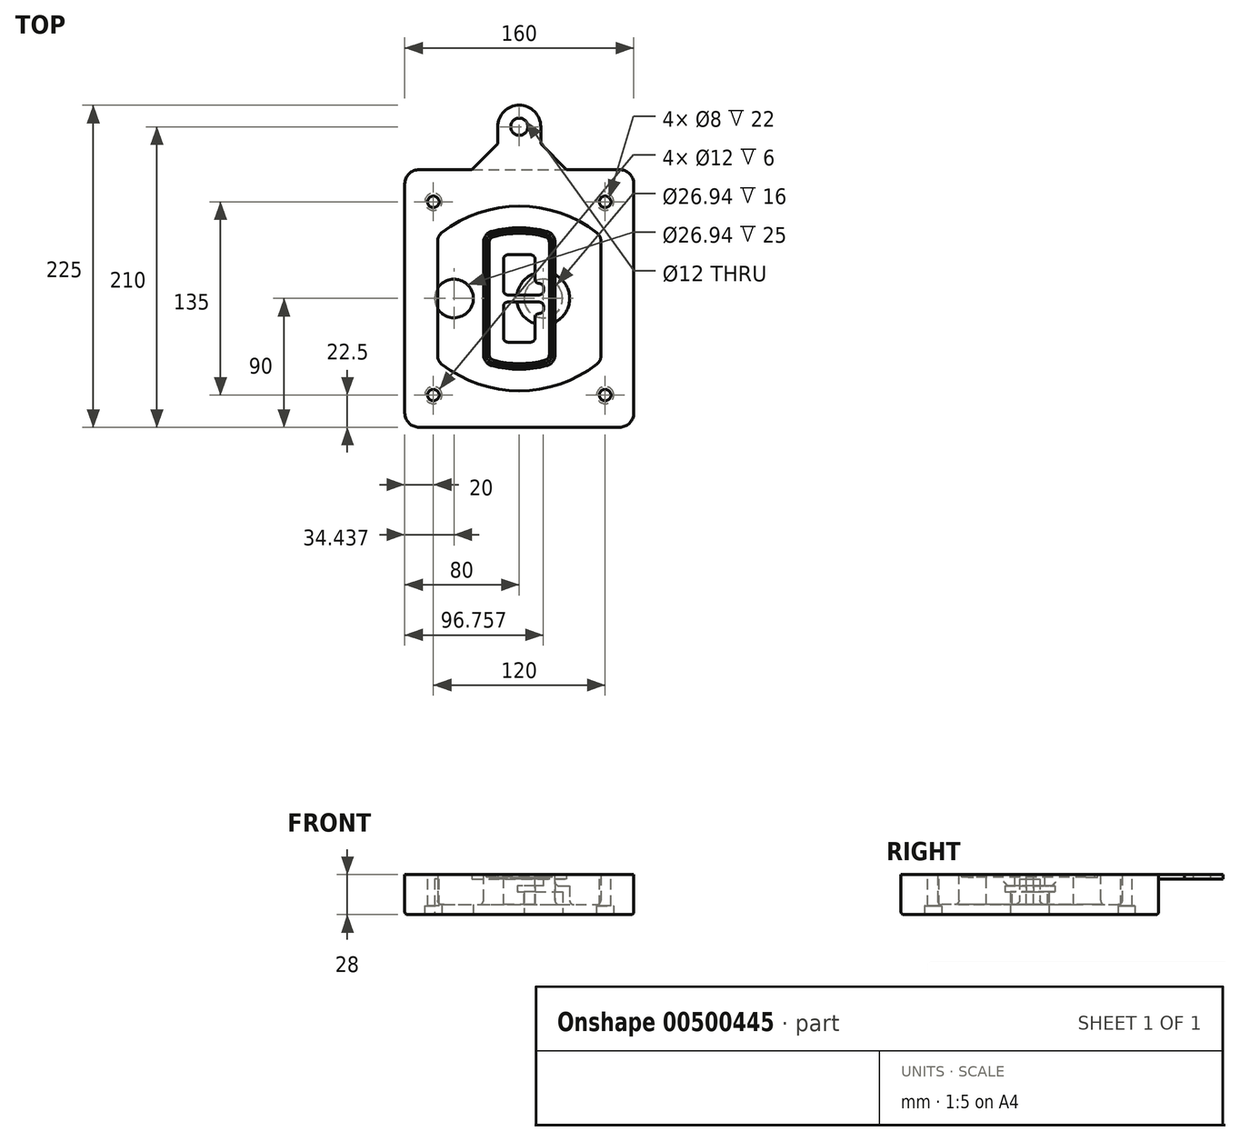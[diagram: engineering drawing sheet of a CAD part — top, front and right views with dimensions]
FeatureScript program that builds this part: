
annotation { "Feature Type Name" : "Feature", "Feature Type Description" : "" }
export const myFeature = defineFeature(function(context is Context, id is Id, definition is map)
    precondition{}
    {
        {
            var Q0;
            Q0=qCreatedBy(makeId("Top.planeOp"),FACE);
            var sketch = newSketch(context, id + "F0", { "sketchPlane" : qUnion([Q0])});
            skPoint(sketch, "E0.rect.middle", {"position": v(0, 0) * mm});
            skLineSegment(sketch, "E1.bottom", {"start": v(-70, -90) * mm, "end": v(70, -90) * mm});
            skLineSegment(sketch, "E1.top", {"start": v(-70, 90) * mm, "end": v(70, 90) * mm});
            skLineSegment(sketch, "E1.left", {"start": v(-80, -80) * mm, "end": v(-80, 80) * mm});
            skLineSegment(sketch, "E1.right", {"start": v(80, -80) * mm, "end": v(80, 80) * mm});
            skLineSegment(sketch, "E2", {"start": v(-80, 90) * mm, "end": v(80, -90) * mm, "construction": true});
            skLineSegment(sketch, "E3", {"start": v(80, 90) * mm, "end": v(-80, -90) * mm, "construction": true});
            skCircle(sketch, "E4", {"center": v(-60, 67.5) * mm, "radius": 4 * mm});
            skCircle(sketch, "E5", {"center": v(60, 67.5) * mm, "radius": 4 * mm});
            skCircle(sketch, "E6", {"center": v(60, -67.5) * mm, "radius": 4 * mm});
            skCircle(sketch, "E7", {"center": v(-60, -67.5) * mm, "radius": 4 * mm});
            skLineSegment(sketch, "E8", {"start": v(-60, 67.5) * mm, "end": v(60, 67.5) * mm, "construction": true});
            skLineSegment(sketch, "E9", {"start": v(60, 67.5) * mm, "end": v(60, -67.5) * mm, "construction": true});
            skLineSegment(sketch, "E10", {"start": v(60, -67.5) * mm, "end": v(-60, -67.5) * mm, "construction": true});
            skLineSegment(sketch, "E11", {"start": v(-60, -67.5) * mm, "end": v(-60, 67.5) * mm, "construction": true});
            skLineSegment(sketch, "E12", {"start": v(-60, 40.3) * mm, "end": v(-60, -40.3) * mm});
            skLineSegment(sketch, "E13", {"start": v(60, 40.3) * mm, "end": v(60, -40.3) * mm});
            skArc(sketch, "E14", {"start": v(56.15, 48.18) * mm, "mid": v(0, 67.5) * mm, "end": v(-56.15, 48.18) * mm});
            skArc(sketch, "E15", {"start": v(-56.15, -48.18) * mm, "mid": v(0, -67.5) * mm, "end": v(56.15, -48.18) * mm});
            skLineSegment(sketch, "E16", {"start": v(-60, 0) * mm, "end": v(60, 0) * mm, "construction": true});
            skPoint(sketch, "E17.visualSharp", {"position": v(-60, -45) * mm});
            skArc(sketch, "E17.filletArc", {"start": v(-60, -40.3) * mm, "mid": v(-58.99, -44.68) * mm, "end": v(-56.15, -48.18) * mm});
            skPoint(sketch, "E18.visualSharp", {"position": v(-60, 45) * mm});
            skArc(sketch, "E18.filletArc", {"start": v(-56.15, 48.18) * mm, "mid": v(-58.99, 44.68) * mm, "end": v(-60, 40.3) * mm});
            skPoint(sketch, "E19.visualSharp", {"position": v(60, 45) * mm});
            skArc(sketch, "E19.filletArc", {"start": v(60, 40.3) * mm, "mid": v(58.99, 44.68) * mm, "end": v(56.15, 48.18) * mm});
            skPoint(sketch, "E20.visualSharp", {"position": v(60, -45) * mm});
            skArc(sketch, "E20.filletArc", {"start": v(56.15, -48.18) * mm, "mid": v(58.99, -44.68) * mm, "end": v(60, -40.3) * mm});
            skPoint(sketch, "E21.visualSharp", {"position": v(-80, 90) * mm});
            skArc(sketch, "E21.filletArc", {"start": v(-70, 90) * mm, "mid": v(-77.07, 87.07) * mm, "end": v(-80, 80) * mm});
            skPoint(sketch, "E22.visualSharp", {"position": v(80, 90) * mm});
            skArc(sketch, "E22.filletArc", {"start": v(80, 80) * mm, "mid": v(77.07, 87.07) * mm, "end": v(70, 90) * mm});
            skPoint(sketch, "E23.visualSharp", {"position": v(80, -90) * mm});
            skArc(sketch, "E23.filletArc", {"start": v(70, -90) * mm, "mid": v(77.07, -87.07) * mm, "end": v(80, -80) * mm});
            skPoint(sketch, "E24.visualSharp", {"position": v(-80, -90) * mm});
            skArc(sketch, "E24.filletArc", {"start": v(-80, -80) * mm, "mid": v(-77.07, -87.07) * mm, "end": v(-70, -90) * mm});
            skArc(sketch, "E25.0", {"start": v(57, 40.3) * mm, "mid": v(56.3, 43.36) * mm, "end": v(54.3, 45.81) * mm});
            skLineSegment(sketch, "E25.1", {"start": v(57, 40.3) * mm, "end": v(57, -40.3) * mm});
            skArc(sketch, "E25.2", {"start": v(54.3, -45.81) * mm, "mid": v(56.3, -43.36) * mm, "end": v(57, -40.3) * mm});
            skArc(sketch, "E25.3", {"start": v(-54.3, -45.81) * mm, "mid": v(0, -64.5) * mm, "end": v(54.3, -45.81) * mm});
            skArc(sketch, "E25.4", {"start": v(-57, -40.3) * mm, "mid": v(-56.3, -43.36) * mm, "end": v(-54.3, -45.81) * mm});
            skArc(sketch, "E25.5", {"start": v(54.3, 45.81) * mm, "mid": v(0, 64.5) * mm, "end": v(-54.3, 45.81) * mm});
            skLineSegment(sketch, "E25.6", {"start": v(-57, 40.3) * mm, "end": v(-57, -40.3) * mm});
            skArc(sketch, "E25.7", {"start": v(-54.3, 45.81) * mm, "mid": v(-56.3, 43.36) * mm, "end": v(-57, 40.3) * mm});
            skArc(sketch, "E26.0", {"start": v(-58.62, 51.33) * mm, "mid": v(-62.58, 46.43) * mm, "end": v(-64, 40.3) * mm});
            skArc(sketch, "E26.1", {"start": v(58.62, 51.33) * mm, "mid": v(0, 71.5) * mm, "end": v(-58.62, 51.33) * mm});
            skArc(sketch, "E26.2", {"start": v(64, 40.3) * mm, "mid": v(62.58, 46.43) * mm, "end": v(58.62, 51.33) * mm});
            skLineSegment(sketch, "E26.3", {"start": v(64, 40.3) * mm, "end": v(64, -40.3) * mm});
            skArc(sketch, "E26.4", {"start": v(58.62, -51.33) * mm, "mid": v(62.58, -46.43) * mm, "end": v(64, -40.3) * mm});
            skLineSegment(sketch, "E26.5", {"start": v(-64, 40.3) * mm, "end": v(-64, -40.3) * mm});
            skArc(sketch, "E26.6", {"start": v(-58.62, -51.33) * mm, "mid": v(0, -71.5) * mm, "end": v(58.62, -51.33) * mm});
            skArc(sketch, "E26.7", {"start": v(-64, -40.3) * mm, "mid": v(-62.58, -46.43) * mm, "end": v(-58.62, -51.33) * mm});
            skSolve(sketch);
        }
        {
            var Q0;
            Q0=makeQuery(id+"F0.imprint","IMPRINT",FACE,{"disambiguationData":[TD([[makeQuery(id+"F0.imprint","IMPRINT",EDGE,{"derivedFrom":sQuery(id+"F0.wireOp",EDGE,"E1.bottom")}),1.0]])]});
            var Q1;
            Q1=makeQuery(id+"F0.imprint","IMPRINT",FACE,{"disambiguationData":[TD([[makeQuery(id+"F0.imprint","IMPRINT",EDGE,{"derivedFrom":sQuery(id+"F0.wireOp",EDGE,"E12")}),1.0]])]});
            var Q2;
            Q2=makeQuery(id+"F0.imprint","IMPRINT",FACE,{"disambiguationData":[TD([[makeQuery(id+"F0.imprint","IMPRINT",EDGE,{"derivedFrom":sQuery(id+"F0.wireOp",EDGE,"E25.0")}),1.0]])]});
            var Q3;
            Q3=makeQuery(id+"F0.imprint","IMPRINT",FACE,{"disambiguationData":[TD([[makeQuery(id+"F0.imprint","IMPRINT",EDGE,{"derivedFrom":sQuery(id+"F0.wireOp",EDGE,"E12")}),-1.0]])]});
            extrude(context, id + "F1", {"entities" : qUnion([Q0, Q1, Q2, Q3]), "oppositeDirection" : true, "depth" : 25 * mm});
        }
        {
            var Q0;
            Q0=makeQuery(id+"F0.imprint","IMPRINT",FACE,{"disambiguationData":[TD([[makeQuery(id+"F0.imprint","IMPRINT",EDGE,{"derivedFrom":sQuery(id+"F0.wireOp",EDGE,"E12")}),1.0]])]});
            extrude(context, id + "F2", {"entities" : qUnion([Q0]), "operationType" : NewBodyOperationType.ADD, "depth" : 3 * mm});
        }
        {
            var Q0;
            Q0=makeQuery(id+"F0.imprint","IMPRINT",FACE,{"disambiguationData":[TD([[makeQuery(id+"F0.imprint","IMPRINT",EDGE,{"derivedFrom":sQuery(id+"F0.wireOp",EDGE,"E25.0")}),1.0]])]});
            extrude(context, id + "F3", {"entities" : qUnion([Q0]), "operationType" : NewBodyOperationType.REMOVE, "oppositeDirection" : true, "depth" : 18 * mm});
        }
        {
            var Q0;
            Q0=makeQuery(id+"F2.opExtrude","CAP_FACE",FACE,{"disambiguationData":[OSD([sQuery(id+"F0.wireOp",EDGE,"E12"),sQuery(id+"F0.wireOp",EDGE,"E13"),sQuery(id+"F0.wireOp",EDGE,"E14"),sQuery(id+"F0.wireOp",EDGE,"E15"),sQuery(id+"F0.wireOp",EDGE,"E17.filletArc"),sQuery(id+"F0.wireOp",EDGE,"E18.filletArc"),sQuery(id+"F0.wireOp",EDGE,"E19.filletArc"),sQuery(id+"F0.wireOp",EDGE,"E20.filletArc"),sQuery(id+"F0.wireOp",EDGE,"E25.0"),sQuery(id+"F0.wireOp",EDGE,"E25.1"),sQuery(id+"F0.wireOp",EDGE,"E25.2"),sQuery(id+"F0.wireOp",EDGE,"E25.3"),sQuery(id+"F0.wireOp",EDGE,"E25.4"),sQuery(id+"F0.wireOp",EDGE,"E25.5"),sQuery(id+"F0.wireOp",EDGE,"E25.6"),sQuery(id+"F0.wireOp",EDGE,"E25.7")])],"isStart":false});
            var sketch = newSketch(context, id + "F4", { "sketchPlane" : qUnion([Q0])});
            skArc(sketch, "E27.0", {"start": v(-19.08, -46.97) * mm, "mid": v(0, -49.5) * mm, "end": v(19.08, -46.97) * mm});
            skArc(sketch, "E28.0", {"start": v(19.08, 46.97) * mm, "mid": v(0, 49.5) * mm, "end": v(-19.08, 46.97) * mm});
            skLineSegment(sketch, "E29", {"start": v(-25, 39.25) * mm, "end": v(-25, -39.25) * mm});
            skLineSegment(sketch, "E30", {"start": v(25, 39.25) * mm, "end": v(25, -39.25) * mm});
            skLineSegment(sketch, "E31", {"start": v(-25, 45.1) * mm, "end": v(25, 45.1) * mm, "construction": true});
            skLineSegment(sketch, "E32", {"start": v(-25, -45.1) * mm, "end": v(25, -45.1) * mm, "construction": true});
            skPoint(sketch, "E33.visualSharp", {"position": v(-25, 45.1) * mm});
            skArc(sketch, "E33.filletArc", {"start": v(-19.08, 46.97) * mm, "mid": v(-23.35, 44.11) * mm, "end": v(-25, 39.25) * mm});
            skPoint(sketch, "E34.visualSharp", {"position": v(25, 45.1) * mm});
            skArc(sketch, "E34.filletArc", {"start": v(25, 39.25) * mm, "mid": v(23.35, 44.11) * mm, "end": v(19.08, 46.97) * mm});
            skPoint(sketch, "E35.visualSharp", {"position": v(25, -45.1) * mm});
            skArc(sketch, "E35.filletArc", {"start": v(19.08, -46.97) * mm, "mid": v(23.35, -44.11) * mm, "end": v(25, -39.25) * mm});
            skPoint(sketch, "E36.visualSharp", {"position": v(-25, -45.1) * mm});
            skArc(sketch, "E36.filletArc", {"start": v(-25, -39.25) * mm, "mid": v(-23.35, -44.11) * mm, "end": v(-19.08, -46.97) * mm});
            skArc(sketch, "E37.0", {"start": v(54.3, 45.81) * mm, "mid": v(0, 64.5) * mm, "end": v(-54.3, 45.81) * mm});
            skArc(sketch, "E37.1", {"start": v(-54.3, 45.81) * mm, "mid": v(-56.3, 43.36) * mm, "end": v(-57, 40.3) * mm});
            skLineSegment(sketch, "E37.2", {"start": v(-57, 40.3) * mm, "end": v(-57, -40.3) * mm});
            skArc(sketch, "E37.3", {"start": v(-57, -40.3) * mm, "mid": v(-56.3, -43.36) * mm, "end": v(-54.3, -45.81) * mm});
            skArc(sketch, "E37.4", {"start": v(-54.3, -45.81) * mm, "mid": v(0, -64.5) * mm, "end": v(54.3, -45.81) * mm});
            skArc(sketch, "E37.5", {"start": v(54.3, -45.81) * mm, "mid": v(56.3, -43.36) * mm, "end": v(57, -40.3) * mm});
            skLineSegment(sketch, "E37.6", {"start": v(57, 40.3) * mm, "end": v(57, -40.3) * mm});
            skArc(sketch, "E37.7", {"start": v(57, 40.3) * mm, "mid": v(56.3, 43.36) * mm, "end": v(54.3, 45.81) * mm});
            skLineSegment(sketch, "E38.0", {"start": v(23, 39.25) * mm, "end": v(23, -39.25) * mm});
            skArc(sketch, "E38.1", {"start": v(18.56, -45.04) * mm, "mid": v(21.76, -42.9) * mm, "end": v(23, -39.25) * mm});
            skArc(sketch, "E38.2", {"start": v(-18.56, -45.04) * mm, "mid": v(0, -47.5) * mm, "end": v(18.56, -45.04) * mm});
            skArc(sketch, "E38.3", {"start": v(-23, -39.25) * mm, "mid": v(-21.76, -42.9) * mm, "end": v(-18.56, -45.04) * mm});
            skLineSegment(sketch, "E38.4", {"start": v(-23, 39.25) * mm, "end": v(-23, -39.25) * mm});
            skArc(sketch, "E38.5", {"start": v(23, 39.25) * mm, "mid": v(21.76, 42.9) * mm, "end": v(18.56, 45.04) * mm});
            skArc(sketch, "E38.6", {"start": v(-18.56, 45.04) * mm, "mid": v(-21.76, 42.9) * mm, "end": v(-23, 39.25) * mm});
            skArc(sketch, "E38.7", {"start": v(18.56, 45.04) * mm, "mid": v(0, 47.5) * mm, "end": v(-18.56, 45.04) * mm});
            skArc(sketch, "E39.0", {"start": v(21, 39.25) * mm, "mid": v(20.18, 41.68) * mm, "end": v(18.04, 43.1) * mm});
            skLineSegment(sketch, "E39.1", {"start": v(21, 39.25) * mm, "end": v(21, -39.25) * mm});
            skArc(sketch, "E39.2", {"start": v(18.04, -43.1) * mm, "mid": v(20.18, -41.68) * mm, "end": v(21, -39.25) * mm});
            skArc(sketch, "E39.3", {"start": v(-18.04, -43.1) * mm, "mid": v(0, -45.5) * mm, "end": v(18.04, -43.1) * mm});
            skArc(sketch, "E39.4", {"start": v(-21, -39.25) * mm, "mid": v(-20.18, -41.68) * mm, "end": v(-18.04, -43.1) * mm});
            skArc(sketch, "E39.5", {"start": v(18.04, 43.1) * mm, "mid": v(0, 45.5) * mm, "end": v(-18.04, 43.1) * mm});
            skLineSegment(sketch, "E39.6", {"start": v(-21, 39.25) * mm, "end": v(-21, -39.25) * mm});
            skArc(sketch, "E39.7", {"start": v(-18.04, 43.1) * mm, "mid": v(-20.18, 41.68) * mm, "end": v(-21, 39.25) * mm});
            skLineSegment(sketch, "E40", {"start": v(-25, 0) * mm, "end": v(25, 0) * mm, "construction": true});
            skLineSegment(sketch, "E41", {"start": v(-11, 5.5) * mm, "end": v(-11, 27.5) * mm});
            skLineSegment(sketch, "E42", {"start": v(-8, 30.5) * mm, "end": v(8, 30.5) * mm});
            skLineSegment(sketch, "E43", {"start": v(11, 27.5) * mm, "end": v(11, 13.5) * mm});
            skLineSegment(sketch, "E44", {"start": v(14, 10.5) * mm, "end": v(14, 10.5) * mm});
            skLineSegment(sketch, "E45", {"start": v(17, 7.5) * mm, "end": v(17, 5.5) * mm});
            skLineSegment(sketch, "E46", {"start": v(14, 2.5) * mm, "end": v(-8, 2.5) * mm});
            skPoint(sketch, "E47.visualSharp", {"position": v(-11, 30.5) * mm});
            skArc(sketch, "E47.filletArc", {"start": v(-8, 30.5) * mm, "mid": v(-10.12, 29.62) * mm, "end": v(-11, 27.5) * mm});
            skPoint(sketch, "E48.visualSharp", {"position": v(11, 30.5) * mm});
            skArc(sketch, "E48.filletArc", {"start": v(11, 27.5) * mm, "mid": v(10.12, 29.62) * mm, "end": v(8, 30.5) * mm});
            skPoint(sketch, "E49.visualSharp", {"position": v(11, 10.5) * mm});
            skArc(sketch, "E49.filletArc", {"start": v(11, 13.5) * mm, "mid": v(11.88, 11.38) * mm, "end": v(14, 10.5) * mm});
            skPoint(sketch, "E50.visualSharp", {"position": v(17, 10.5) * mm});
            skArc(sketch, "E50.filletArc", {"start": v(17, 7.5) * mm, "mid": v(16.12, 9.62) * mm, "end": v(14, 10.5) * mm});
            skPoint(sketch, "E51.visualSharp", {"position": v(17, 2.5) * mm});
            skArc(sketch, "E51.filletArc", {"start": v(14, 2.5) * mm, "mid": v(16.12, 3.38) * mm, "end": v(17, 5.5) * mm});
            skPoint(sketch, "E52.visualSharp", {"position": v(-11, 2.5) * mm});
            skArc(sketch, "E52.filletArc", {"start": v(-11, 5.5) * mm, "mid": v(-10.12, 3.38) * mm, "end": v(-8, 2.5) * mm});
            skLineSegment(sketch, "E53.0.MirrorCS", {"start": v(14, -2.5) * mm, "end": v(-8, -2.5) * mm});
            skArc(sketch, "E54.0.MirrorCS", {"start": v(-11, -5.5) * mm, "mid": v(-10.12, -3.38) * mm, "end": v(-8, -2.5) * mm});
            skLineSegment(sketch, "E55.0.MirrorCS", {"start": v(-11, -5.5) * mm, "end": v(-11, -27.5) * mm});
            skArc(sketch, "E56.0.MirrorCS", {"start": v(-8, -30.5) * mm, "mid": v(-10.12, -29.62) * mm, "end": v(-11, -27.5) * mm});
            skLineSegment(sketch, "E57.0.MirrorCS", {"start": v(-8, -30.5) * mm, "end": v(8, -30.5) * mm});
            skArc(sketch, "E58.0.MirrorCS", {"start": v(11, -27.5) * mm, "mid": v(10.12, -29.62) * mm, "end": v(8, -30.5) * mm});
            skLineSegment(sketch, "E59.0.MirrorCS", {"start": v(11, -27.5) * mm, "end": v(11, -13.5) * mm});
            skArc(sketch, "E60.0.MirrorCS", {"start": v(11, -13.5) * mm, "mid": v(11.88, -11.38) * mm, "end": v(14, -10.5) * mm});
            skArc(sketch, "E61.0.MirrorCS", {"start": v(17, -7.5) * mm, "mid": v(16.12, -9.62) * mm, "end": v(14, -10.5) * mm});
            skLineSegment(sketch, "E62.0.MirrorCS", {"start": v(17, -7.5) * mm, "end": v(17, -5.5) * mm});
            skArc(sketch, "E63.0.MirrorCS", {"start": v(14, -2.5) * mm, "mid": v(16.12, -3.38) * mm, "end": v(17, -5.5) * mm});
            skSolve(sketch);
        }
        {
            var Q0;
            Q0=makeQuery(id+"F4.imprint","IMPRINT",FACE,{"disambiguationData":[TD([[makeQuery(id+"F4.imprint","IMPRINT",EDGE,{"derivedFrom":sQuery(id+"F4.wireOp",EDGE,"E27.0")}),1.0]])]});
            var Q1;
            Q1=makeQuery(id+"F4.imprint","IMPRINT",FACE,{"disambiguationData":[TD([[makeQuery(id+"F4.imprint","IMPRINT",EDGE,{"derivedFrom":sQuery(id+"F4.wireOp",EDGE,"E38.0")}),-1.0]])]});
            var Q2;
            Q2=makeQuery(id+"F4.imprint","IMPRINT",FACE,{"disambiguationData":[TD([[makeQuery(id+"F4.imprint","IMPRINT",EDGE,{"derivedFrom":sQuery(id+"F4.wireOp",EDGE,"E39.0")}),1.0]])]});
            extrude(context, id + "F5", {"entities" : qUnion([Q0, Q1, Q2]), "operationType" : NewBodyOperationType.ADD, "endBound" : BoundingType.UP_TO_NEXT, "oppositeDirection" : true, "depth" : 25 * mm});
        }
        {
            var Q0;
            Q0=makeQuery(id+"F4.imprint","IMPRINT",FACE,{"disambiguationData":[TD([[makeQuery(id+"F4.imprint","IMPRINT",EDGE,{"derivedFrom":sQuery(id+"F4.wireOp",EDGE,"E38.0")}),-1.0]])]});
            extrude(context, id + "F6", {"entities" : qUnion([Q0]), "operationType" : NewBodyOperationType.REMOVE, "oppositeDirection" : true, "depth" : 2 * mm});
        }
        {
            var Q0;
            Q0=makeQuery(id+"F1.opExtrude","CAP_FACE",FACE,{"disambiguationData":[OSD([sQuery(id+"F0.wireOp",EDGE,"E1.bottom"),sQuery(id+"F0.wireOp",EDGE,"E1.top"),sQuery(id+"F0.wireOp",EDGE,"E1.left"),sQuery(id+"F0.wireOp",EDGE,"E1.right"),sQuery(id+"F0.wireOp",EDGE,"E4"),sQuery(id+"F0.wireOp",EDGE,"E5"),sQuery(id+"F0.wireOp",EDGE,"E6"),sQuery(id+"F0.wireOp",EDGE,"E7"),sQuery(id+"F0.wireOp",EDGE,"E21.filletArc"),sQuery(id+"F0.wireOp",EDGE,"E22.filletArc"),sQuery(id+"F0.wireOp",EDGE,"E23.filletArc"),sQuery(id+"F0.wireOp",EDGE,"E24.filletArc")])],"isStart":false});
            var sketch = newSketch(context, id + "F7", { "sketchPlane" : qUnion([Q0])});
            skCircle(sketch, "E64", {"center": v(16.76, 0) * mm, "radius": 13.47 * mm});
            skCircle(sketch, "E65", {"center": v(-45.56, 0) * mm, "radius": 13.47 * mm});
            skLineSegment(sketch, "E66", {"start": v(80, 0) * mm, "end": v(-80, 0) * mm});
            skCircle(sketch, "E67", {"center": v(16.76, 0) * mm, "radius": 18.47 * mm});
            skCircle(sketch, "E68", {"center": v(60, -67.5) * mm, "radius": 6 * mm});
            skCircle(sketch, "E69", {"center": v(-60, -67.5) * mm, "radius": 6 * mm});
            skCircle(sketch, "E70", {"center": v(-60, 67.5) * mm, "radius": 6 * mm});
            skCircle(sketch, "E71", {"center": v(60, 67.5) * mm, "radius": 6 * mm});
            skSolve(sketch);
        }
        {
            var Q0;
            {var subQ1=sQuery(id+"F7.wireOp",EDGE,"E66");var subQ4=sQuery(id+"F7.wireOp",EDGE,"E64");var subQ6=makeQuery(id+"F7.imprint","INTERSECT",VERTEX,{"disambiguationData":[OD(0.0)],"derivedFrom":[subQ4,subQ1]});Q0=makeQuery(id+"F7.imprint","IMPRINT",FACE,{"disambiguationData":[TD([[makeQuery(id+"F7.imprint","IMPRINT",EDGE,{"disambiguationData":[TD([[subQ6,-1.0]])],"derivedFrom":subQ4}),-1.0]])]});}
            var Q1;
            {var subQ0=sQuery(id+"F7.wireOp",EDGE,"E66");var subQ1=sQuery(id+"F7.wireOp",EDGE,"E64");var subQ3=makeQuery(id+"F7.imprint","INTERSECT",VERTEX,{"disambiguationData":[OD(0.0)],"derivedFrom":[subQ1,subQ0]});Q1=makeQuery(id+"F7.imprint","IMPRINT",FACE,{"disambiguationData":[TD([[makeQuery(id+"F7.imprint","IMPRINT",EDGE,{"disambiguationData":[TD([[subQ3,-1.0]])],"derivedFrom":subQ1}),1.0]])]});}
            var Q2;
            {var subQ0=sQuery(id+"F7.wireOp",EDGE,"E66");var subQ1=sQuery(id+"F7.wireOp",EDGE,"E64");var subQ3=makeQuery(id+"F7.imprint","INTERSECT",VERTEX,{"disambiguationData":[OD(0.0)],"derivedFrom":[subQ1,subQ0]});Q2=makeQuery(id+"F7.imprint","IMPRINT",FACE,{"disambiguationData":[TD([[makeQuery(id+"F7.imprint","IMPRINT",EDGE,{"disambiguationData":[TD([[subQ3,1.0]])],"derivedFrom":subQ1}),1.0]])]});}
            var Q3;
            {var subQ1=sQuery(id+"F7.wireOp",EDGE,"E66");var subQ4=sQuery(id+"F7.wireOp",EDGE,"E64");var subQ6=makeQuery(id+"F7.imprint","INTERSECT",VERTEX,{"disambiguationData":[OD(0.0)],"derivedFrom":[subQ4,subQ1]});Q3=makeQuery(id+"F7.imprint","IMPRINT",FACE,{"disambiguationData":[TD([[makeQuery(id+"F7.imprint","IMPRINT",EDGE,{"disambiguationData":[TD([[subQ6,1.0]])],"derivedFrom":subQ4}),-1.0]])]});}
            extrude(context, id + "F8", {"entities" : qUnion([Q0, Q1, Q2, Q3]), "operationType" : NewBodyOperationType.ADD, "oppositeDirection" : true, "depth" : 20 * mm});
        }
        {
            var Q0;
            {var subQ0=sQuery(id+"F7.wireOp",EDGE,"E66");var subQ1=sQuery(id+"F7.wireOp",EDGE,"E64");var subQ3=makeQuery(id+"F7.imprint","INTERSECT",VERTEX,{"disambiguationData":[OD(0.0)],"derivedFrom":[subQ1,subQ0]});Q0=makeQuery(id+"F7.imprint","IMPRINT",FACE,{"disambiguationData":[TD([[makeQuery(id+"F7.imprint","IMPRINT",EDGE,{"disambiguationData":[TD([[subQ3,-1.0]])],"derivedFrom":subQ1}),1.0]])]});}
            var Q1;
            {var subQ0=sQuery(id+"F7.wireOp",EDGE,"E66");var subQ1=sQuery(id+"F7.wireOp",EDGE,"E64");var subQ3=makeQuery(id+"F7.imprint","INTERSECT",VERTEX,{"disambiguationData":[OD(0.0)],"derivedFrom":[subQ1,subQ0]});Q1=makeQuery(id+"F7.imprint","IMPRINT",FACE,{"disambiguationData":[TD([[makeQuery(id+"F7.imprint","IMPRINT",EDGE,{"disambiguationData":[TD([[subQ3,1.0]])],"derivedFrom":subQ1}),1.0]])]});}
            extrude(context, id + "F9", {"entities" : qUnion([Q0, Q1]), "operationType" : NewBodyOperationType.REMOVE, "oppositeDirection" : true, "depth" : 16 * mm});
        }
        {
            var Q0;
            {var subQ0=sQuery(id+"F7.wireOp",EDGE,"E66");var subQ1=sQuery(id+"F7.wireOp",EDGE,"E65");var subQ3=makeQuery(id+"F7.imprint","INTERSECT",VERTEX,{"disambiguationData":[OD(0.0)],"derivedFrom":[subQ1,subQ0]});Q0=makeQuery(id+"F7.imprint","IMPRINT",FACE,{"disambiguationData":[TD([[makeQuery(id+"F7.imprint","IMPRINT",EDGE,{"disambiguationData":[TD([[subQ3,-1.0]])],"derivedFrom":subQ1}),1.0]])]});}
            var Q1;
            {var subQ0=sQuery(id+"F7.wireOp",EDGE,"E66");var subQ1=sQuery(id+"F7.wireOp",EDGE,"E65");var subQ3=makeQuery(id+"F7.imprint","INTERSECT",VERTEX,{"disambiguationData":[OD(0.0)],"derivedFrom":[subQ1,subQ0]});Q1=makeQuery(id+"F7.imprint","IMPRINT",FACE,{"disambiguationData":[TD([[makeQuery(id+"F7.imprint","IMPRINT",EDGE,{"disambiguationData":[TD([[subQ3,1.0]])],"derivedFrom":subQ1}),1.0]])]});}
            extrude(context, id + "F10", {"entities" : qUnion([Q0, Q1]), "operationType" : NewBodyOperationType.REMOVE, "oppositeDirection" : true, "depth" : 25 * mm});
        }
        {
            var Q0;
            Q0=makeQuery(id+"F7.imprint","IMPRINT",FACE,{"disambiguationData":[TD([[makeQuery(id+"F7.imprint","IMPRINT",EDGE,{"derivedFrom":sQuery(id+"F7.wireOp",EDGE,"E68")}),1.0]])]});
            var Q1;
            Q1=makeQuery(id+"F7.imprint","IMPRINT",FACE,{"disambiguationData":[TD([[makeQuery(id+"F7.imprint","IMPRINT",EDGE,{"derivedFrom":makeQuery(id+"F1.opExtrude","CAP_EDGE",EDGE,{"disambiguationData":[OSD([sQuery(id+"F0.wireOp",EDGE,"E5")])],"isStart":false})}),-1.0]])]});
            var Q2;
            Q2=makeQuery(id+"F7.imprint","IMPRINT",FACE,{"disambiguationData":[TD([[makeQuery(id+"F7.imprint","IMPRINT",EDGE,{"derivedFrom":sQuery(id+"F7.wireOp",EDGE,"E69")}),1.0]])]});
            var Q3;
            Q3=makeQuery(id+"F7.imprint","IMPRINT",FACE,{"disambiguationData":[TD([[makeQuery(id+"F7.imprint","IMPRINT",EDGE,{"derivedFrom":makeQuery(id+"F1.opExtrude","CAP_EDGE",EDGE,{"disambiguationData":[OSD([sQuery(id+"F0.wireOp",EDGE,"E4")])],"isStart":false})}),-1.0]])]});
            var Q4;
            Q4=makeQuery(id+"F7.imprint","IMPRINT",FACE,{"disambiguationData":[TD([[makeQuery(id+"F7.imprint","IMPRINT",EDGE,{"derivedFrom":sQuery(id+"F7.wireOp",EDGE,"E70")}),1.0]])]});
            var Q5;
            Q5=makeQuery(id+"F7.imprint","IMPRINT",FACE,{"disambiguationData":[TD([[makeQuery(id+"F7.imprint","IMPRINT",EDGE,{"derivedFrom":makeQuery(id+"F1.opExtrude","CAP_EDGE",EDGE,{"disambiguationData":[OSD([sQuery(id+"F0.wireOp",EDGE,"E7")])],"isStart":false})}),-1.0]])]});
            var Q6;
            Q6=makeQuery(id+"F7.imprint","IMPRINT",FACE,{"disambiguationData":[TD([[makeQuery(id+"F7.imprint","IMPRINT",EDGE,{"derivedFrom":sQuery(id+"F7.wireOp",EDGE,"E71")}),1.0]])]});
            var Q7;
            Q7=makeQuery(id+"F7.imprint","IMPRINT",FACE,{"disambiguationData":[TD([[makeQuery(id+"F7.imprint","IMPRINT",EDGE,{"derivedFrom":makeQuery(id+"F1.opExtrude","CAP_EDGE",EDGE,{"disambiguationData":[OSD([sQuery(id+"F0.wireOp",EDGE,"E6")])],"isStart":false})}),-1.0]])]});
            extrude(context, id + "F11", {"entities" : qUnion([Q0, Q1, Q2, Q3, Q4, Q5, Q6, Q7]), "operationType" : NewBodyOperationType.REMOVE, "oppositeDirection" : true, "depth" : 6 * mm});
        }
        {
            var Q0;
            Q0=makeQuery(id+"F9.boolean.opBoolean","COPY",FACE,{"derivedFrom":makeQuery(id+"F9.opExtrude","CAP_FACE",FACE,{"disambiguationData":[OSD([sQuery(id+"F7.wireOp",EDGE,"E64")])],"isStart":false})});
            var sketch = newSketch(context, id + "F12", { "sketchPlane" : qUnion([Q0])});
            skArc(sketch, "E72.0", {"start": v(11, 17.55) * mm, "mid": v(2.57, 11.82) * mm, "end": v(-1.54, 2.5) * mm});
            skArc(sketch, "E72.1", {"start": v(-1.54, -2.5) * mm, "mid": v(2.57, -11.82) * mm, "end": v(11, -17.55) * mm});
            skLineSegment(sketch, "E73", {"start": v(-1.54, -2.5) * mm, "end": v(14, -2.5) * mm});
            skLineSegment(sketch, "E74.0", {"start": v(14, 2.5) * mm, "end": v(-1.54, 2.5) * mm});
            skArc(sketch, "E74.1", {"start": v(14, 2.5) * mm, "mid": v(16.12, 3.38) * mm, "end": v(17, 5.5) * mm});
            skLineSegment(sketch, "E74.2", {"start": v(17, 7.5) * mm, "end": v(17, 5.5) * mm});
            skArc(sketch, "E74.3", {"start": v(17, 7.5) * mm, "mid": v(16.12, 9.62) * mm, "end": v(14, 10.5) * mm});
            skArc(sketch, "E74.4", {"start": v(11, 13.5) * mm, "mid": v(11.88, 11.38) * mm, "end": v(14, 10.5) * mm});
            skLineSegment(sketch, "E74.5", {"start": v(11, 17.55) * mm, "end": v(11, 13.5) * mm});
            skLineSegment(sketch, "E74.7", {"start": v(14, -2.5) * mm, "end": v(-1.54, -2.5) * mm});
            skArc(sketch, "E74.8", {"start": v(14, -2.5) * mm, "mid": v(16.12, -3.38) * mm, "end": v(17, -5.5) * mm});
            skLineSegment(sketch, "E74.9", {"start": v(17, -7.5) * mm, "end": v(17, -5.5) * mm});
            skArc(sketch, "E74.10", {"start": v(17, -7.5) * mm, "mid": v(16.12, -9.62) * mm, "end": v(14, -10.5) * mm});
            skArc(sketch, "E74.11", {"start": v(11, -13.5) * mm, "mid": v(11.88, -11.38) * mm, "end": v(14, -10.5) * mm});
            skLineSegment(sketch, "E74.12", {"start": v(11, -17.55) * mm, "end": v(11, -13.5) * mm});
            skPoint(sketch, "E75.orphan", {"position": v(11, -27.5) * mm});
            skPoint(sketch, "E76.orphan", {"position": v(-8, -2.5) * mm});
            skPoint(sketch, "E77.orphan", {"position": v(-8, 2.5) * mm});
            skPoint(sketch, "E78.orphan", {"position": v(11, 27.5) * mm});
            skSolve(sketch);
        }
        {
            var Q0;
            {var subQ7=sQuery(id+"F12.wireOp",EDGE,"E72.0");var subQ14=sQuery(id+"F12.wireOp",EDGE,"E72.1");var subQ16=sQuery(id+"F12.wireOp",EDGE,"E74.1");var subQ18=sQuery(id+"F12.wireOp",EDGE,"E74.8");Q0=qUnion([makeQuery(id+"F12.imprint","IMPRINT",FACE,{"disambiguationData":[TD([[makeQuery(id+"F12.imprint","IMPRINT",EDGE,{"derivedFrom":subQ7}),1.0]])]}),makeQuery(id+"F12.imprint","IMPRINT",FACE,{"disambiguationData":[TD([[makeQuery(id+"F12.imprint","IMPRINT",EDGE,{"derivedFrom":subQ14}),1.0]])]}),makeQuery(id+"F12.imprint","IMPRINT",FACE,{"disambiguationData":[TD([[makeQuery(id+"F12.imprint","IMPRINT",EDGE,{"derivedFrom":subQ16}),1.0]])]}),makeQuery(id+"F12.imprint","IMPRINT",FACE,{"disambiguationData":[TD([[makeQuery(id+"F12.imprint","IMPRINT",EDGE,{"derivedFrom":subQ18}),-1.0]])]})]);}
            var Q1;
            Q1=makeQuery(id+"F5.boolean.opBoolean","SPLIT",FACE,{"disambiguationData":[TD([makeQuery(id+"F5.opExtrude","SWEPT_FACE",FACE,{"disambiguationData":[OSD([sQuery(id+"F4.wireOp",EDGE,"E41")])]})])],"derivedFrom":makeQuery(id+"F3.boolean.opBoolean","COPY",FACE,{"derivedFrom":makeQuery(id+"F3.opExtrude","CAP_FACE",FACE,{"disambiguationData":[OSD([sQuery(id+"F0.wireOp",EDGE,"E25.0"),sQuery(id+"F0.wireOp",EDGE,"E25.1"),sQuery(id+"F0.wireOp",EDGE,"E25.2"),sQuery(id+"F0.wireOp",EDGE,"E25.3"),sQuery(id+"F0.wireOp",EDGE,"E25.4"),sQuery(id+"F0.wireOp",EDGE,"E25.5"),sQuery(id+"F0.wireOp",EDGE,"E25.6"),sQuery(id+"F0.wireOp",EDGE,"E25.7")])],"isStart":false})})});
            extrude(context, id + "F13", {"entities" : qUnion([Q0]), "operationType" : NewBodyOperationType.REMOVE, "endBound" : BoundingType.UP_TO_SURFACE, "endBoundEntityFace" : qUnion([Q1]), "depth" : 25 * mm});
        }
        {
            var Q0;
            Q0=makeQuery(id+"F3.boolean.opBoolean","COPY",EDGE,{"derivedFrom":makeQuery(id+"F3.opExtrude","CAP_EDGE",EDGE,{"disambiguationData":[OSD([sQuery(id+"F0.wireOp",EDGE,"E25.6")])],"isStart":false})});
            var Q1;
            Q1=makeQuery(id+"F8.boolean.opBoolean","INTERSECT",EDGE,{"derivedFrom":[makeQuery(id+"F5.opExtrude","SWEPT_FACE",FACE,{"disambiguationData":[OSD([sQuery(id+"F4.wireOp",EDGE,"E30")])]}),makeQuery(id+"F8.opExtrude","CAP_FACE",FACE,{"disambiguationData":[OSD([sQuery(id+"F7.wireOp",EDGE,"E67")])],"isStart":false})]});
            var Q2;
            Q2=makeQuery(id+"F8.boolean.opBoolean","INTERSECT",EDGE,{"disambiguationData":[OD(1.0)],"derivedFrom":[makeQuery(id+"F5.opExtrude","SWEPT_FACE",FACE,{"disambiguationData":[OSD([sQuery(id+"F4.wireOp",EDGE,"E30")])]}),makeQuery(id+"F8.opExtrude","SWEPT_FACE",FACE,{"disambiguationData":[OSD([sQuery(id+"F7.wireOp",EDGE,"E67")])]})]});
            var Q3;
            {var subQ0=sQuery(id+"F4.wireOp",EDGE,"E30");Q3=makeQuery(id+"F8.boolean.opBoolean","SPLIT",EDGE,{"disambiguationData":[TD([makeQuery(id+"F5.opExtrude","SWEPT_FACE",FACE,{"disambiguationData":[OSD([sQuery(id+"F4.wireOp",EDGE,"E35.filletArc")])]})])],"derivedFrom":makeQuery(id+"F5.opExtrude","CAP_EDGE",EDGE,{"disambiguationData":[OSD([subQ0])],"isStart":false})});}
            var Q4;
            {var subQ0=sQuery(id+"F0.wireOp",EDGE,"E25.7");var subQ1=sQuery(id+"F0.wireOp",EDGE,"E25.1");var subQ2=sQuery(id+"F0.wireOp",EDGE,"E25.6");var subQ3=sQuery(id+"F0.wireOp",EDGE,"E25.5");var subQ4=sQuery(id+"F0.wireOp",EDGE,"E25.4");var subQ5=sQuery(id+"F0.wireOp",EDGE,"E25.0");var subQ6=sQuery(id+"F0.wireOp",EDGE,"E25.2");var subQ7=sQuery(id+"F0.wireOp",EDGE,"E25.3");Q4=makeQuery(id+"F8.boolean.opBoolean","INTERSECT",EDGE,{"derivedFrom":[makeQuery(id+"F5.boolean.opBoolean","SPLIT",FACE,{"disambiguationData":[TD([makeQuery(id+"F2.opExtrude","SWEPT_FACE",FACE,{"disambiguationData":[OSD([subQ5])]})])],"derivedFrom":makeQuery(id+"F3.boolean.opBoolean","COPY",FACE,{"derivedFrom":makeQuery(id+"F3.opExtrude","CAP_FACE",FACE,{"disambiguationData":[OSD([subQ5,subQ1,subQ6,subQ7,subQ4,subQ3,subQ2,subQ0])],"isStart":false})})}),makeQuery(id+"F8.opExtrude","SWEPT_FACE",FACE,{"disambiguationData":[OSD([sQuery(id+"F7.wireOp",EDGE,"E67")])]})]});}
            var Q5;
            Q5=makeQuery(id+"F8.boolean.opBoolean","INTERSECT",EDGE,{"disambiguationData":[OD(0.0)],"derivedFrom":[makeQuery(id+"F5.opExtrude","SWEPT_FACE",FACE,{"disambiguationData":[OSD([sQuery(id+"F4.wireOp",EDGE,"E30")])]}),makeQuery(id+"F8.opExtrude","SWEPT_FACE",FACE,{"disambiguationData":[OSD([sQuery(id+"F7.wireOp",EDGE,"E67")])]})]});
            fillet(context, id + "F14", {"entities" : qUnion([Q0, Q1, Q2, Q3, Q4, Q5]), "radius" : 3 * mm, "tangentPropagation" : true, "allowEdgeOverflow" : false});
        }
        {
            var Q0;
            Q0=makeQuery(id+"F1.opExtrude","CAP_EDGE",EDGE,{"disambiguationData":[OSD([sQuery(id+"F0.wireOp",EDGE,"E1.bottom")])],"isStart":false});
            fillet(context, id + "F15", {"entities" : qUnion([Q0]), "radius" : 2 * mm, "tangentPropagation" : true, "allowEdgeOverflow" : false});
        }
        {
            var Q0;
            {var subQ0=sQuery(id+"F0.wireOp",EDGE,"E21.filletArc");var subQ1=sQuery(id+"F0.wireOp",EDGE,"E7");var subQ2=sQuery(id+"F0.wireOp",EDGE,"E6");var subQ3=sQuery(id+"F0.wireOp",EDGE,"E5");var subQ4=sQuery(id+"F0.wireOp",EDGE,"E4");var subQ5=sQuery(id+"F0.wireOp",EDGE,"E22.filletArc");var subQ6=sQuery(id+"F0.wireOp",EDGE,"E1.bottom");var subQ7=sQuery(id+"F0.wireOp",EDGE,"E1.right");var subQ8=sQuery(id+"F0.wireOp",EDGE,"E1.top");var subQ9=sQuery(id+"F0.wireOp",EDGE,"E1.left");var subQ10=sQuery(id+"F0.wireOp",EDGE,"E23.filletArc");var subQ11=sQuery(id+"F0.wireOp",EDGE,"E24.filletArc");Q0=makeQuery(id+"F2.boolean.opBoolean","SPLIT",FACE,{"disambiguationData":[TD([makeQuery(id+"F1.opExtrude","SWEPT_FACE",FACE,{"disambiguationData":[OSD([subQ6])]})])],"derivedFrom":makeQuery(id+"F1.opExtrude","CAP_FACE",FACE,{"disambiguationData":[OSD([subQ6,subQ8,subQ9,subQ7,subQ4,subQ3,subQ2,subQ1,subQ0,subQ5,subQ10,subQ11])],"isStart":true})});}
            var sketch = newSketch(context, id + "F16", { "sketchPlane" : qUnion([Q0])});
            skLineSegment(sketch, "E79", {"start": v(0, 90) * mm, "end": v(0, 120) * mm, "construction": true});
            skCircle(sketch, "E80", {"center": v(0, 120) * mm, "radius": 6 * mm});
            skLineSegment(sketch, "E81", {"start": v(-33, 90) * mm, "end": v(-15, 108) * mm});
            skLineSegment(sketch, "E82", {"start": v(-15, 108) * mm, "end": v(-15, 120) * mm});
            skLineSegment(sketch, "E83", {"start": v(33, 90) * mm, "end": v(15, 108) * mm});
            skLineSegment(sketch, "E84", {"start": v(15, 120) * mm, "end": v(15, 108) * mm});
            skArc(sketch, "E85", {"start": v(15, 120) * mm, "mid": v(0, 135) * mm, "end": v(-15, 120) * mm});
            skLineSegment(sketch, "E86", {"start": v(-80, 0) * mm, "end": v(80, 0) * mm, "construction": true});
            skPoint(sketch, "E87", {"position": v(22.24, 127.9) * mm});
            skArc(sketch, "E88.MirrorCS", {"start": v(15, -120) * mm, "mid": v(0, -135) * mm, "end": v(-15, -120) * mm});
            skLineSegment(sketch, "E89.MirrorCS", {"start": v(-15, -108) * mm, "end": v(-15, -120) * mm});
            skLineSegment(sketch, "E90.MirrorCS", {"start": v(15, -120) * mm, "end": v(15, -108) * mm});
            skLineSegment(sketch, "E91.MirrorCS", {"start": v(33, -90) * mm, "end": v(15, -108) * mm});
            skLineSegment(sketch, "E92.MirrorCS", {"start": v(-33, -90) * mm, "end": v(-15, -108) * mm});
            skCircle(sketch, "E93.MirrorC", {"center": v(0, -120) * mm, "radius": 6 * mm});
            skSolve(sketch);
        }
        {
            var Q0;
            Q0=makeQuery(id+"F16.imprint","IMPRINT",FACE,{"disambiguationData":[TD([[makeQuery(id+"F16.imprint","IMPRINT",EDGE,{"derivedFrom":sQuery(id+"F16.wireOp",EDGE,"E80")}),-1.0]])]});
            var Q1;
            Q1=makeQuery(id+"F16.imprint","IMPRINT",FACE,{"disambiguationData":[TD([[makeQuery(id+"F16.imprint","IMPRINT",EDGE,{"derivedFrom":makeQuery(id+"F1.opExtrude","CAP_EDGE",EDGE,{"disambiguationData":[OSD([sQuery(id+"F0.wireOp",EDGE,"E1.left")])],"isStart":true})}),-1.0]])]});
            var Q2;
            Q2=makeQuery(id+"F16.imprint","IMPRINT",FACE,{"disambiguationData":[TD([[makeQuery(id+"F16.imprint","IMPRINT",EDGE,{"derivedFrom":sQuery(id+"F16.wireOp",EDGE,"E88.MirrorCS")}),-1.0]])]});
            var Q3;
            {var subQ0=sQuery(id+"F4.wireOp",EDGE,"E36.filletArc");var subQ1=sQuery(id+"F4.wireOp",EDGE,"E35.filletArc");var subQ2=sQuery(id+"F4.wireOp",EDGE,"E34.filletArc");var subQ3=sQuery(id+"F4.wireOp",EDGE,"E33.filletArc");var subQ4=sQuery(id+"F4.wireOp",EDGE,"E27.0");var subQ5=sQuery(id+"F4.wireOp",EDGE,"E30");var subQ6=sQuery(id+"F4.wireOp",EDGE,"E28.0");var subQ7=sQuery(id+"F4.wireOp",EDGE,"E29");Q3=makeQuery(id+"F6.boolean.opBoolean","SPLIT",FACE,{"disambiguationData":[TD([makeQuery(id+"F5.opExtrude","SWEPT_FACE",FACE,{"disambiguationData":[OSD([subQ4])]})])],"derivedFrom":makeQuery(id+"F5.opExtrude","CAP_FACE",FACE,{"disambiguationData":[OSD([subQ4,subQ6,subQ7,subQ5,subQ3,subQ2,subQ1,subQ0,sQuery(id+"F4.wireOp",EDGE,"E41"),sQuery(id+"F4.wireOp",EDGE,"E42"),sQuery(id+"F4.wireOp",EDGE,"E43"),sQuery(id+"F4.wireOp",EDGE,"E45"),sQuery(id+"F4.wireOp",EDGE,"E46"),sQuery(id+"F4.wireOp",EDGE,"E47.filletArc"),sQuery(id+"F4.wireOp",EDGE,"E48.filletArc"),sQuery(id+"F4.wireOp",EDGE,"E49.filletArc"),sQuery(id+"F4.wireOp",EDGE,"E50.filletArc"),sQuery(id+"F4.wireOp",EDGE,"E51.filletArc"),sQuery(id+"F4.wireOp",EDGE,"E52.filletArc"),sQuery(id+"F4.wireOp",EDGE,"E53.0.MirrorCS"),sQuery(id+"F4.wireOp",EDGE,"E54.0.MirrorCS"),sQuery(id+"F4.wireOp",EDGE,"E55.0.MirrorCS"),sQuery(id+"F4.wireOp",EDGE,"E56.0.MirrorCS"),sQuery(id+"F4.wireOp",EDGE,"E57.0.MirrorCS"),sQuery(id+"F4.wireOp",EDGE,"E58.0.MirrorCS"),sQuery(id+"F4.wireOp",EDGE,"E59.0.MirrorCS"),sQuery(id+"F4.wireOp",EDGE,"E60.0.MirrorCS"),sQuery(id+"F4.wireOp",EDGE,"E61.0.MirrorCS"),sQuery(id+"F4.wireOp",EDGE,"E62.0.MirrorCS"),sQuery(id+"F4.wireOp",EDGE,"E63.0.MirrorCS")])],"isStart":true})});}
            extrude(context, id + "F17", {"entities" : qUnion([Q0, Q1, Q2]), "operationType" : NewBodyOperationType.ADD, "endBound" : BoundingType.UP_TO_SURFACE, "endBoundEntityFace" : qUnion([Q3]), "depth" : 25 * mm});
        }
    });
